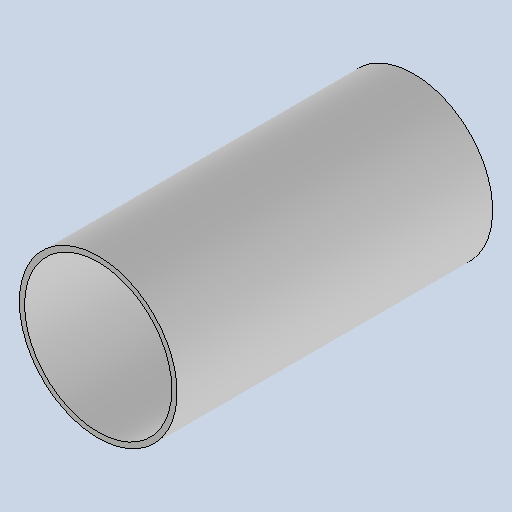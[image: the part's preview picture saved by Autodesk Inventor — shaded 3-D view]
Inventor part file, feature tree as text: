
AUTODESK INVENTOR PART (.ipt)
format: ipt  version: 2025.1 (Build 291241020, 241B)  size: 145,408 bytes
history: native  units: mm
features: extrude x1, sketch x1
ambient origin geometry x8: Origin, YZ Plane, XZ Plane, XY Plane, X Axis, Y Axis, Z Axis, Center Point
bodies: Solid1 (feature_tree)
feature tree (2):
  extrude  "Extrusion1"  Depth=180.0mm
  sketch  "Sketch1"  dims[d0=90.0mm d1=3.0mm d2=180.0mm d3=0.0mm]
